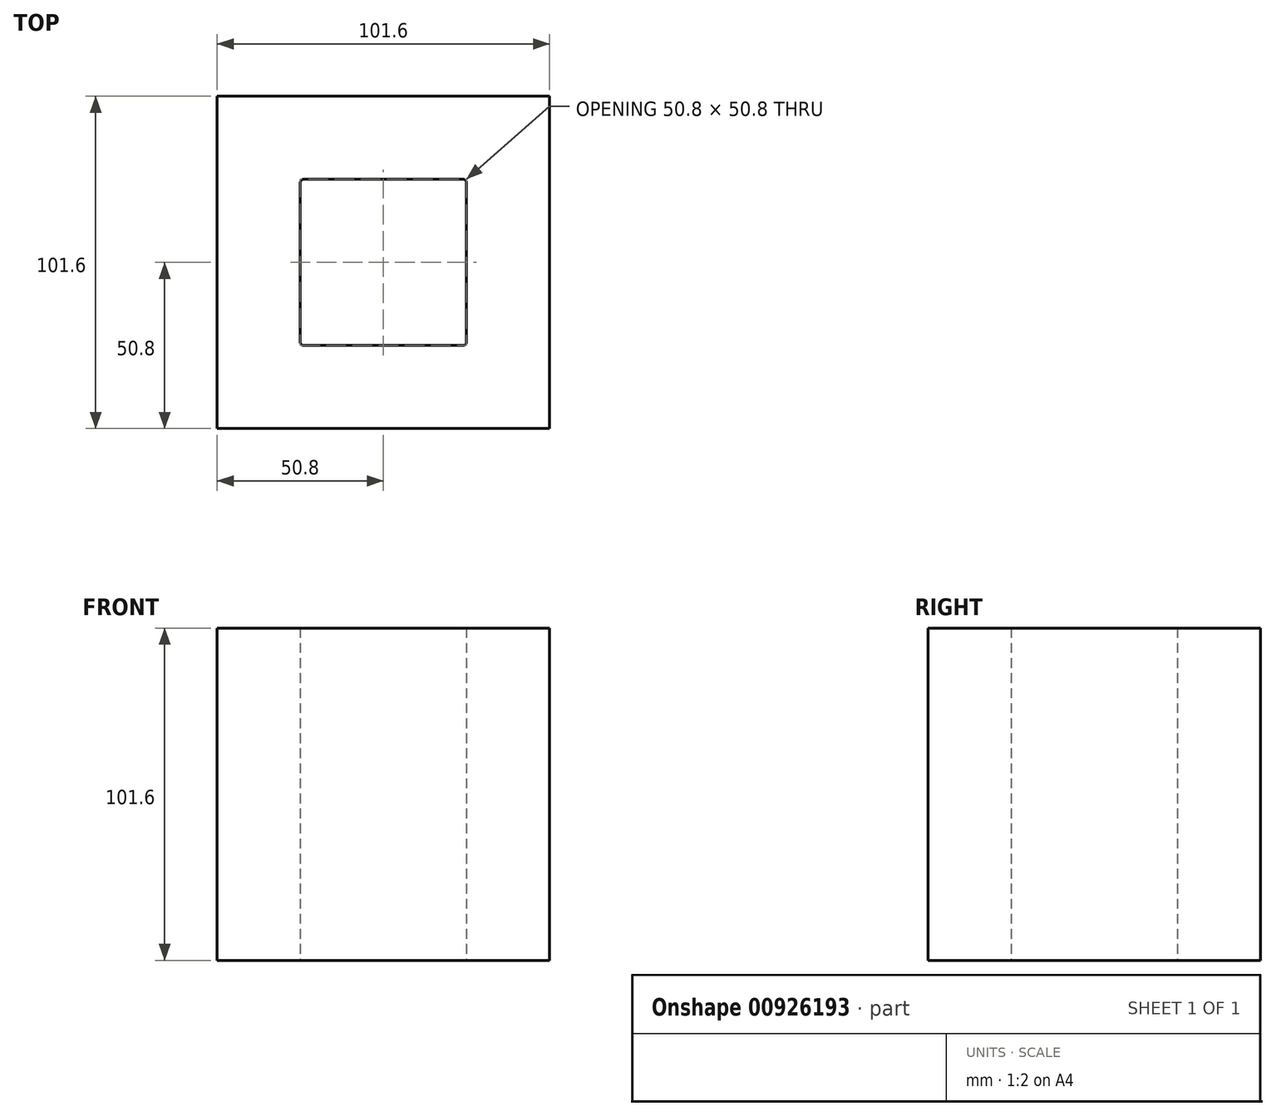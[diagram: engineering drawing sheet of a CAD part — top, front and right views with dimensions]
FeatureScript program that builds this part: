
annotation { "Feature Type Name" : "Feature", "Feature Type Description" : "" }
export const myFeature = defineFeature(function(context is Context, id is Id, definition is map)
    precondition{}
    {
        {
            var Q0;
            Q0=qCreatedBy(makeId("Front.planeOp"),FACE);
            var sketch = newSketch(context, id + "F0", { "sketchPlane" : qUnion([Q0])});
            skLineSegment(sketch, "E0.bottom", {"start": v(50.8, 50.8) * mm, "end": v(-50.8, 50.8) * mm});
            skLineSegment(sketch, "E0.top", {"start": v(50.8, -50.8) * mm, "end": v(-50.8, -50.8) * mm});
            skLineSegment(sketch, "E0.left", {"start": v(50.8, 50.8) * mm, "end": v(50.8, -50.8) * mm});
            skLineSegment(sketch, "E0.right", {"start": v(-50.8, 50.8) * mm, "end": v(-50.8, -50.8) * mm});
            skPoint(sketch, "E0.middle", {"position": v(0, 0) * mm});
            skSolve(sketch);
        }
        {
            var Q0;
            Q0 = qSketchRegion(id + "F0", true);
            extrude(context, id + "F1", {"entities" : qUnion([Q0]), "depth" : 101.6 * mm, "offsetDistance" : 25.4 * mm, "symmetric" : true});
        }
        {
            var Q0;
            Q0=qCreatedBy(makeId("Top.planeOp"),FACE);
            var sketch = newSketch(context, id + "F2", { "sketchPlane" : qUnion([Q0])});
            skLineSegment(sketch, "E1.bottom", {"start": v(25.4, 25.4) * mm, "end": v(-25.4, 25.4) * mm});
            skLineSegment(sketch, "E1.top", {"start": v(25.4, -25.4) * mm, "end": v(-25.4, -25.4) * mm});
            skLineSegment(sketch, "E1.left", {"start": v(25.4, 25.4) * mm, "end": v(25.4, -25.4) * mm});
            skLineSegment(sketch, "E1.right", {"start": v(-25.4, 25.4) * mm, "end": v(-25.4, -25.4) * mm});
            skPoint(sketch, "E1.middle", {"position": v(0, 0) * mm});
            skSolve(sketch);
        }
        {
            var Q0;
            Q0 = qSketchRegion(id + "F2", true);
            extrude(context, id + "F3", {"entities" : qUnion([Q0]), "operationType" : NewBodyOperationType.REMOVE, "depth" : 101.6 * mm, "offsetDistance" : 25.4 * mm, "symmetric" : true});
        }
        {
            var Q0;
            Q0=makeQuery(id+"F3.boolean.opBoolean","COPY",EDGE,{"derivedFrom":makeQuery(id+"F3.opExtrude","SWEPT_EDGE",EDGE,{"disambiguationData":[OSD([sQuery(id+"F2.wireOp",EDGE,"E1.top"),sQuery(id+"F2.wireOp",EDGE,"E1.right")])]})});
            var Q1;
            Q1=makeQuery(id+"F3.boolean.opBoolean","COPY",EDGE,{"derivedFrom":makeQuery(id+"F3.opExtrude","SWEPT_EDGE",EDGE,{"disambiguationData":[OSD([sQuery(id+"F2.wireOp",EDGE,"E1.bottom"),sQuery(id+"F2.wireOp",EDGE,"E1.right")])]})});
            var Q2;
            Q2=makeQuery(id+"F3.boolean.opBoolean","COPY",EDGE,{"derivedFrom":makeQuery(id+"F3.opExtrude","SWEPT_EDGE",EDGE,{"disambiguationData":[OSD([sQuery(id+"F2.wireOp",EDGE,"E1.bottom"),sQuery(id+"F2.wireOp",EDGE,"E1.left")])]})});
            var Q3;
            Q3=makeQuery(id+"F3.boolean.opBoolean","COPY",EDGE,{"derivedFrom":makeQuery(id+"F3.opExtrude","SWEPT_EDGE",EDGE,{"disambiguationData":[OSD([sQuery(id+"F2.wireOp",EDGE,"E1.top"),sQuery(id+"F2.wireOp",EDGE,"E1.left")])]})});
            fillet(context, id + "F4", {"entities" : qUnion([Q0, Q1, Q2, Q3]), "radius" : 1.02 * mm, "tangentPropagation" : true, "allowEdgeOverflow" : false});
        }
    });
